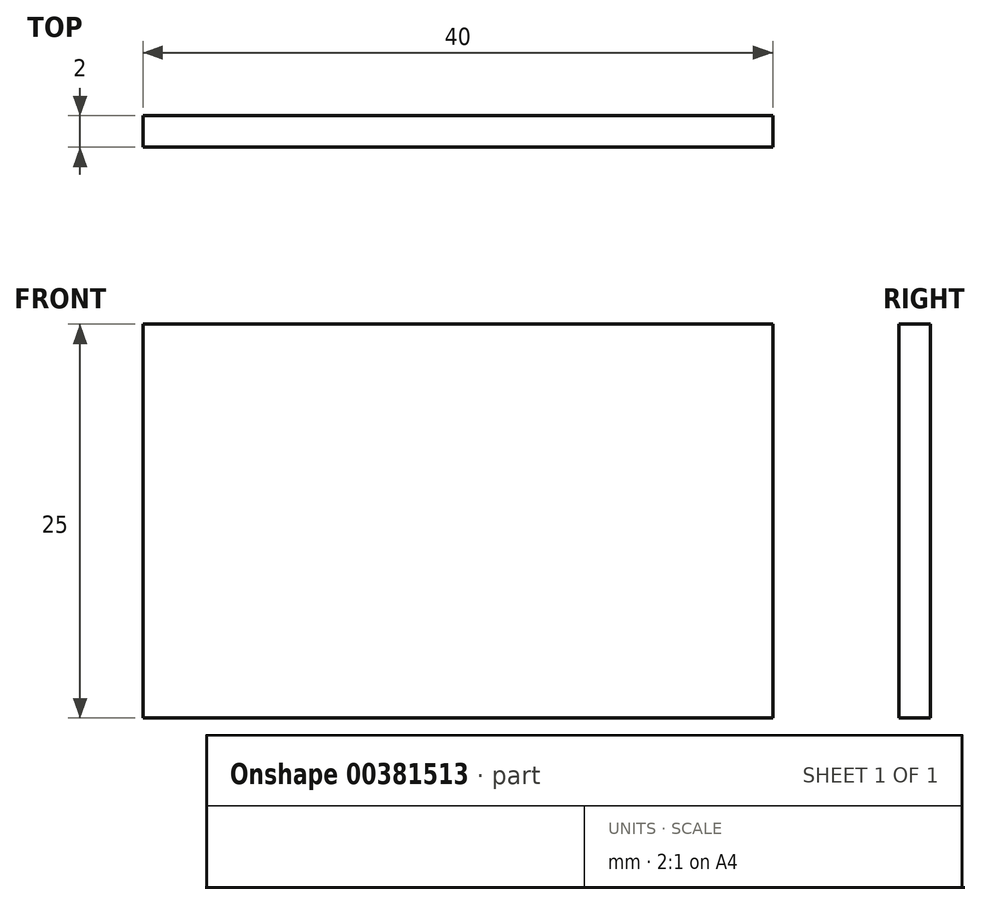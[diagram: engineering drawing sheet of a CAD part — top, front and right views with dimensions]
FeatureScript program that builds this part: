
annotation { "Feature Type Name" : "Feature", "Feature Type Description" : "" }
export const myFeature = defineFeature(function(context is Context, id is Id, definition is map)
    precondition{}
    {
        {
            var Q0;
            Q0=qCreatedBy(makeId("Top.planeOp"),FACE);
            var sketch = newSketch(context, id + "F0", { "sketchPlane" : qUnion([Q0])});
            skLineSegment(sketch, "E0.bottom", {"start": v(20, -1) * mm, "end": v(-20, -1) * mm});
            skLineSegment(sketch, "E0.top", {"start": v(20, 1) * mm, "end": v(-20, 1) * mm});
            skLineSegment(sketch, "E0.left", {"start": v(20, -1) * mm, "end": v(20, 1) * mm});
            skLineSegment(sketch, "E0.right", {"start": v(-20, -1) * mm, "end": v(-20, 1) * mm});
            skPoint(sketch, "E0.middle", {"position": v(0, 0) * mm});
            skSolve(sketch);
        }
        {
            var Q0;
            Q0=makeQuery(id+"F0.imprint","IMPRINT",FACE,{"disambiguationData":[TD([[makeQuery(id+"F0.imprint","IMPRINT",EDGE,{"derivedFrom":sQuery(id+"F0.wireOp",EDGE,"E0.bottom")}),-1.0]])]});
            extrude(context, id + "F1", {"entities" : qUnion([Q0]), "depth" : 25 * mm});
        }
    });
